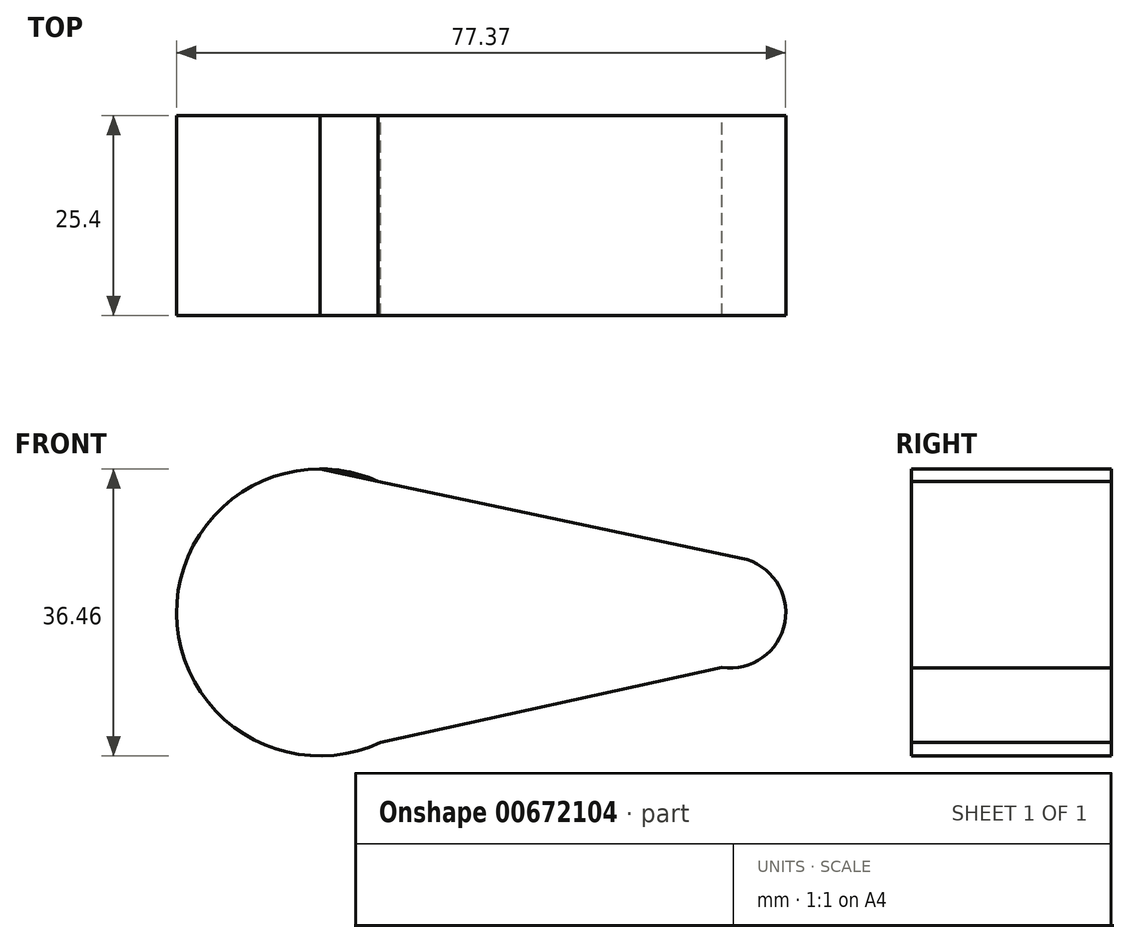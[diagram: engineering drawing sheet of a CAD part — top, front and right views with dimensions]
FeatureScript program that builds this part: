
annotation { "Feature Type Name" : "Feature", "Feature Type Description" : "" }
export const myFeature = defineFeature(function(context is Context, id is Id, definition is map)
    precondition{}
    {
        {
            var Q0;
            Q0=qCreatedBy(makeId("Front.planeOp"),FACE);
            var sketch = newSketch(context, id + "F0", { "sketchPlane" : qUnion([Q0])});
            skCircle(sketch, "E0", {"center": v(0, 0) * mm, "radius": 18.23 * mm});
            skCircle(sketch, "E1", {"center": v(52.1, 0) * mm, "radius": 7.05 * mm});
            skLineSegment(sketch, "E2", {"start": v(0, 18.23) * mm, "end": v(53.56, 6.9) * mm});
            skLineSegment(sketch, "E3", {"start": v(0, -18.23) * mm, "end": v(51.03, -6.96) * mm});
            skSolve(sketch);
        }
        {
            var Q0;
            Q0=qCreatedBy(makeId("Front.planeOp"),FACE);
            var sketch = newSketch(context, id + "F1", { "sketchPlane" : qUnion([Q0])});
            skCircle(sketch, "E4", {"center": v(0, 0) * mm, "radius": 8.9 * mm});
            skSolve(sketch);
        }
        {
            var Q0;
            Q0=sQuery(id+"F1.wireOp",EDGE,"E4");
            extrude(context, id + "F2", {"bodyType" : ToolBodyType.SURFACE, "surfaceEntities" : qUnion([Q0]), "depth" : 25.4 * mm, "offsetDistance" : 25.4 * mm});
        }
        {
            var Q0;
            {var subQ0=sQuery(id+"F0.wireOp",EDGE,"E2");var subQ1=sQuery(id+"F0.wireOp",EDGE,"E0");var subQ2=makeQuery(id+"F0.imprint","INTERSECT",VERTEX,{"disambiguationData":[OD(0.0)],"derivedFrom":[subQ1,subQ0]});Q0=makeQuery(id+"F0.imprint","IMPRINT",FACE,{"disambiguationData":[TD([[makeQuery(id+"F0.imprint","IMPRINT",EDGE,{"disambiguationData":[TD([[subQ2,-1.0]])],"derivedFrom":subQ1}),1.0]])]});}
            var sketch = newSketch(context, id + "F3", { "sketchPlane" : qUnion([Q0])});
            skSolve(sketch);
        }
        {
            var Q0;
            {var subQ0=sQuery(id+"F0.wireOp",EDGE,"E2");var subQ1=sQuery(id+"F0.wireOp",EDGE,"E0");var subQ2=makeQuery(id+"F0.imprint","INTERSECT",VERTEX,{"disambiguationData":[OD(0.0)],"derivedFrom":[subQ1,subQ0]});Q0=makeQuery(id+"F3.imprint","IMPRINT",FACE,{"disambiguationData":[TD([[makeQuery(id+"F3.imprint","IMPRINT",EDGE,{"derivedFrom":makeQuery(id+"F0.imprint","IMPRINT",EDGE,{"disambiguationData":[TD([[subQ2,-1.0]])],"derivedFrom":subQ1})}),1.0]])]});}
            var Q1;
            {var subQ0=sQuery(id+"F0.wireOp",EDGE,"E1");var subQ1=makeQuery(id+"F0.imprint","INTERSECT",VERTEX,{"derivedFrom":[subQ0,sQuery(id+"F0.wireOp",EDGE,"E2")]});Q1=makeQuery(id+"F0.imprint","IMPRINT",FACE,{"disambiguationData":[TD([[makeQuery(id+"F0.imprint","IMPRINT",EDGE,{"disambiguationData":[TD([[subQ1,-1.0]])],"derivedFrom":subQ0}),1.0]])]});}
            var Q2;
            {var subQ0=sQuery(id+"F0.wireOp",EDGE,"E2");var subQ1=sQuery(id+"F0.wireOp",EDGE,"E0");var subQ2=makeQuery(id+"F0.imprint","INTERSECT",VERTEX,{"disambiguationData":[OD(1.0)],"derivedFrom":[subQ1,subQ0]});Q2=makeQuery(id+"F0.imprint","IMPRINT",FACE,{"disambiguationData":[TD([[makeQuery(id+"F0.imprint","IMPRINT",EDGE,{"disambiguationData":[TD([[subQ2,1.0]])],"derivedFrom":subQ1}),-1.0]])]});}
            var Q3;
            Q3 = qSketchRegion(id + "F0", true);
            extrude(context, id + "F4", {"entities" : qUnion([Q0, Q1, Q2, Q3]), "depth" : 25.4 * mm, "offsetDistance" : 25.4 * mm});
        }
        {
            var Q0;
            Q0=qCreatedBy(makeId("Front.planeOp"),FACE);
            var sketch = newSketch(context, id + "F5", { "sketchPlane" : qUnion([Q0])});
            skCircle(sketch, "E5", {"center": v(48.36, 0) * mm, "radius": 5.63 * mm});
            skSolve(sketch);
        }
        {
            var Q0;
            Q0=sQuery(id+"F5.wireOp",EDGE,"E5");
            extrude(context, id + "F6", {"bodyType" : ToolBodyType.SURFACE, "surfaceEntities" : qUnion([Q0]), "depth" : 25.4 * mm, "offsetDistance" : 25.4 * mm});
        }
    });
